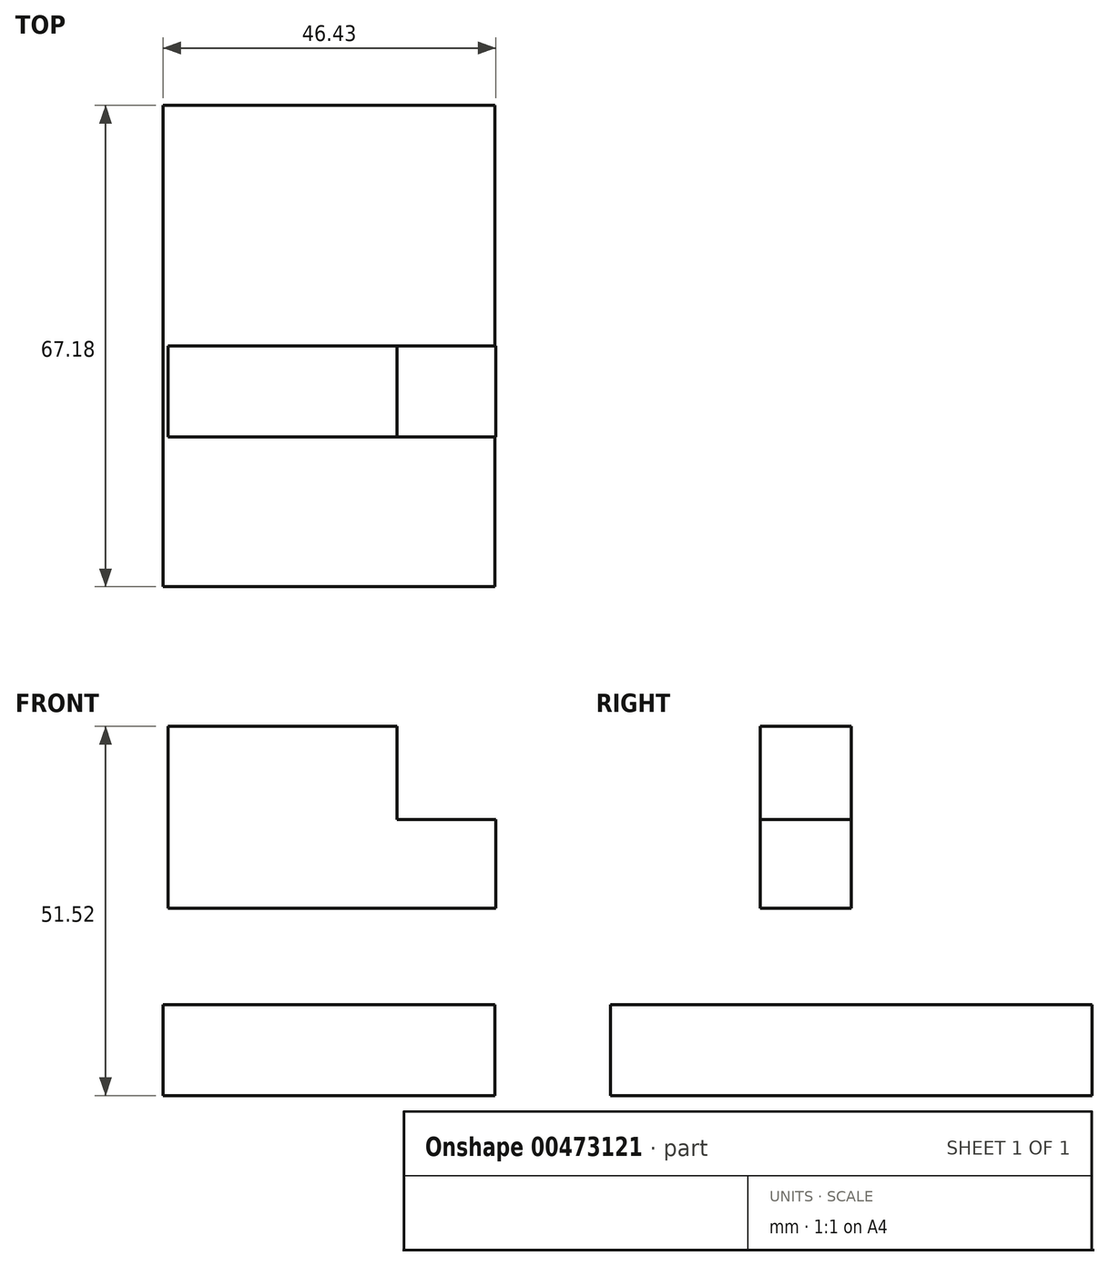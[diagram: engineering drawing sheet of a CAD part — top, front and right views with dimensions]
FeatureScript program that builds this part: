
annotation { "Feature Type Name" : "Feature", "Feature Type Description" : "" }
export const myFeature = defineFeature(function(context is Context, id is Id, definition is map)
    precondition{}
    {
        {
            var Q0;
            Q0=qCreatedBy(makeId("Top.planeOp"),FACE);
            var sketch = newSketch(context, id + "F0", { "sketchPlane" : qUnion([Q0])});
            skLineSegment(sketch, "E0.bottom", {"start": v(-23.17, 33.6) * mm, "end": v(23.17, 33.6) * mm});
            skLineSegment(sketch, "E0.top", {"start": v(-23.17, -33.6) * mm, "end": v(23.17, -33.6) * mm});
            skLineSegment(sketch, "E0.left", {"start": v(-23.17, 33.6) * mm, "end": v(-23.17, -33.6) * mm});
            skLineSegment(sketch, "E0.right", {"start": v(23.17, 33.6) * mm, "end": v(23.17, -33.6) * mm});
            skPoint(sketch, "E0.middle", {"position": v(0, 0) * mm});
            skSolve(sketch);
        }
        {
            var Q0;
            Q0=makeQuery(id+"F0.imprint","IMPRINT",FACE,{"disambiguationData":[TD([[makeQuery(id+"F0.imprint","IMPRINT",EDGE,{"derivedFrom":sQuery(id+"F0.wireOp",EDGE,"E0.bottom")}),-1.0]])]});
            extrude(context, id + "F1", {"entities" : qUnion([Q0]), "depth" : 12.7 * mm});
        }
        {
            var Q0;
            Q0=qCreatedBy(makeId("Front.planeOp"),FACE);
            var sketch = newSketch(context, id + "F2", { "sketchPlane" : qUnion([Q0])});
            skLineSegment(sketch, "E1.bottom", {"start": v(23.26, 51.52) * mm, "end": v(-22.46, 51.52) * mm});
            skLineSegment(sketch, "E1.top", {"start": v(23.26, 26.12) * mm, "end": v(-22.46, 26.12) * mm});
            skLineSegment(sketch, "E1.left", {"start": v(23.26, 51.52) * mm, "end": v(23.26, 26.12) * mm});
            skLineSegment(sketch, "E1.right", {"start": v(-22.46, 51.52) * mm, "end": v(-22.46, 26.12) * mm});
            skPoint(sketch, "E1.middle", {"position": v(0.4, 38.82) * mm});
            skSolve(sketch);
        }
        {
            var Q0;
            Q0 = qSketchRegion(id + "F2", true);
            extrude(context, id + "F3", {"entities" : qUnion([Q0]), "depth" : 12.7 * mm});
        }
        {
            var Q0;
            Q0=makeQuery(id+"F3.opExtrude","CAP_FACE",FACE,{"disambiguationData":[OSD([sQuery(id+"F2.wireOp",EDGE,"E1.bottom"),sQuery(id+"F2.wireOp",EDGE,"E1.top"),sQuery(id+"F2.wireOp",EDGE,"E1.left"),sQuery(id+"F2.wireOp",EDGE,"E1.right")])],"isStart":true});
            var sketch = newSketch(context, id + "F4", { "sketchPlane" : qUnion([Q0])});
            skLineSegment(sketch, "E2.bottom", {"start": v(-23.26, 51.52) * mm, "end": v(-9.48, 51.52) * mm});
            skLineSegment(sketch, "E2.top", {"start": v(-23.26, 38.5) * mm, "end": v(-9.48, 38.5) * mm});
            skLineSegment(sketch, "E2.left", {"start": v(-23.26, 51.52) * mm, "end": v(-23.26, 38.5) * mm});
            skLineSegment(sketch, "E2.right", {"start": v(-9.48, 51.52) * mm, "end": v(-9.48, 38.5) * mm});
            skSolve(sketch);
        }
        {
            var Q0;
            Q0 = qSketchRegion(id + "F4", true);
            extrude(context, id + "F5", {"entities" : qUnion([Q0]), "operationType" : NewBodyOperationType.REMOVE, "oppositeDirection" : true, "depth" : 25.4 * mm});
        }
    });
